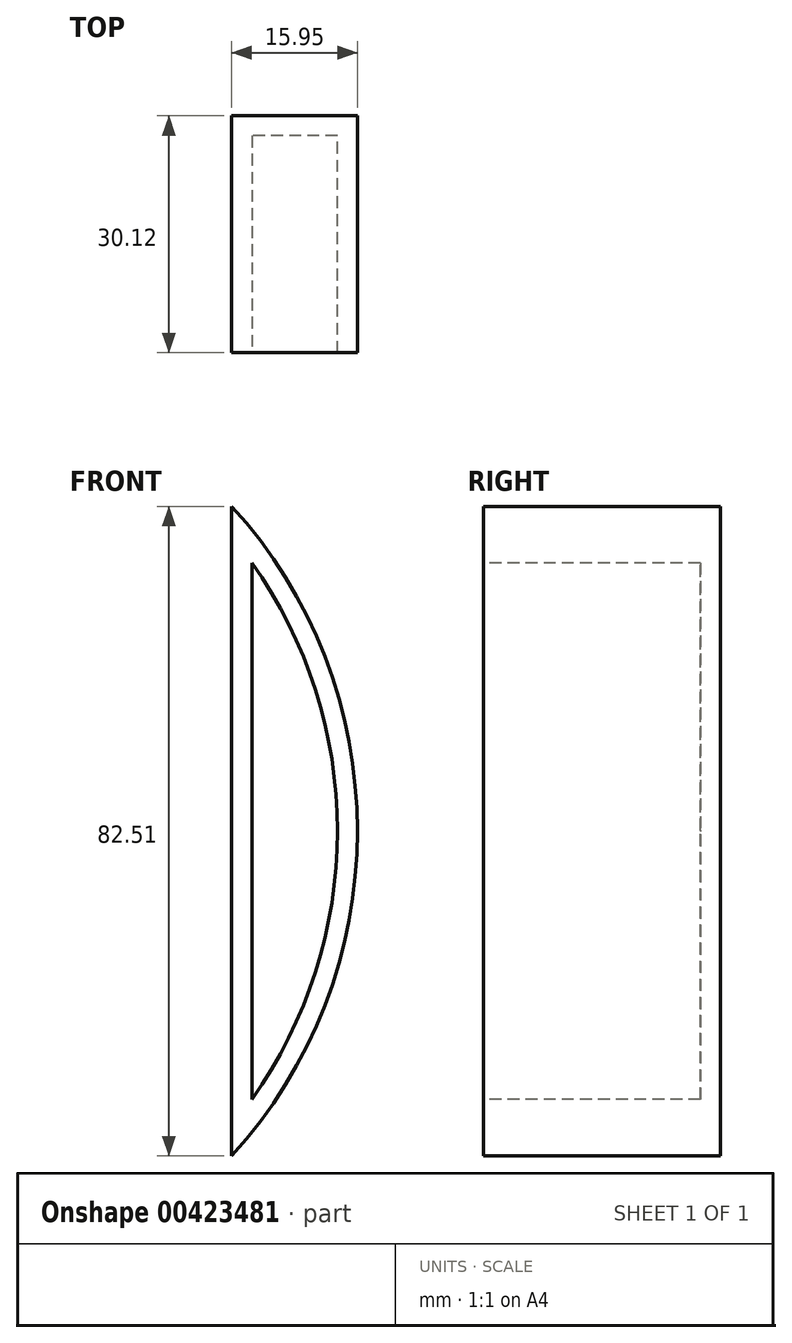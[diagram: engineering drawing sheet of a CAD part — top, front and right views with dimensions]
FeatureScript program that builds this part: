
annotation { "Feature Type Name" : "Feature", "Feature Type Description" : "" }
export const myFeature = defineFeature(function(context is Context, id is Id, definition is map)
    precondition{}
    {
        {
            var Q0;
            Q0=qCreatedBy(makeId("Top.planeOp"),FACE);
            var sketch = newSketch(context, id + "F0", { "sketchPlane" : qUnion([Q0])});
            skLineSegment(sketch, "E0.bottom", {"start": v(15.95, 18.8) * mm, "end": v(0, 18.8) * mm});
            skLineSegment(sketch, "E0.top", {"start": v(15.95, 48.92) * mm, "end": v(0, 48.92) * mm});
            skLineSegment(sketch, "E0.left", {"start": v(15.95, 18.8) * mm, "end": v(15.95, 48.92) * mm});
            skLineSegment(sketch, "E0.right", {"start": v(0, 18.8) * mm, "end": v(0, 48.92) * mm});
            skSolve(sketch);
        }
        {
            var Q0;
            Q0 = qSketchRegion(id + "F0", true);
            extrude(context, id + "F1", {"entities" : qUnion([Q0]), "depth" : 82.51 * mm});
        }
        {
            var Q0;
            Q0=makeQuery(id+"F1.opExtrude","CAP_EDGE",EDGE,{"disambiguationData":[OSD([sQuery(id+"F0.wireOp",EDGE,"E0.left")])],"isStart":false});
            var Q1;
            Q1=makeQuery(id+"F1.opExtrude","CAP_EDGE",EDGE,{"disambiguationData":[OSD([sQuery(id+"F0.wireOp",EDGE,"E0.left")])],"isStart":true});
            fillet(context, id + "F2", {"entities" : qUnion([Q0, Q1]), "radius" : 61.15 * mm, "tangentPropagation" : true, "allowEdgeOverflow" : false});
        }
        {
            var Q0;
            Q0=makeQuery(id+"F1.opExtrude","SWEPT_FACE",FACE,{"disambiguationData":[OSD([sQuery(id+"F0.wireOp",EDGE,"E0.bottom")])]});
            shell(context, id + "F3", {"entities" : qUnion([Q0]), "thickness" : 2.54 * mm});
        }
    });
